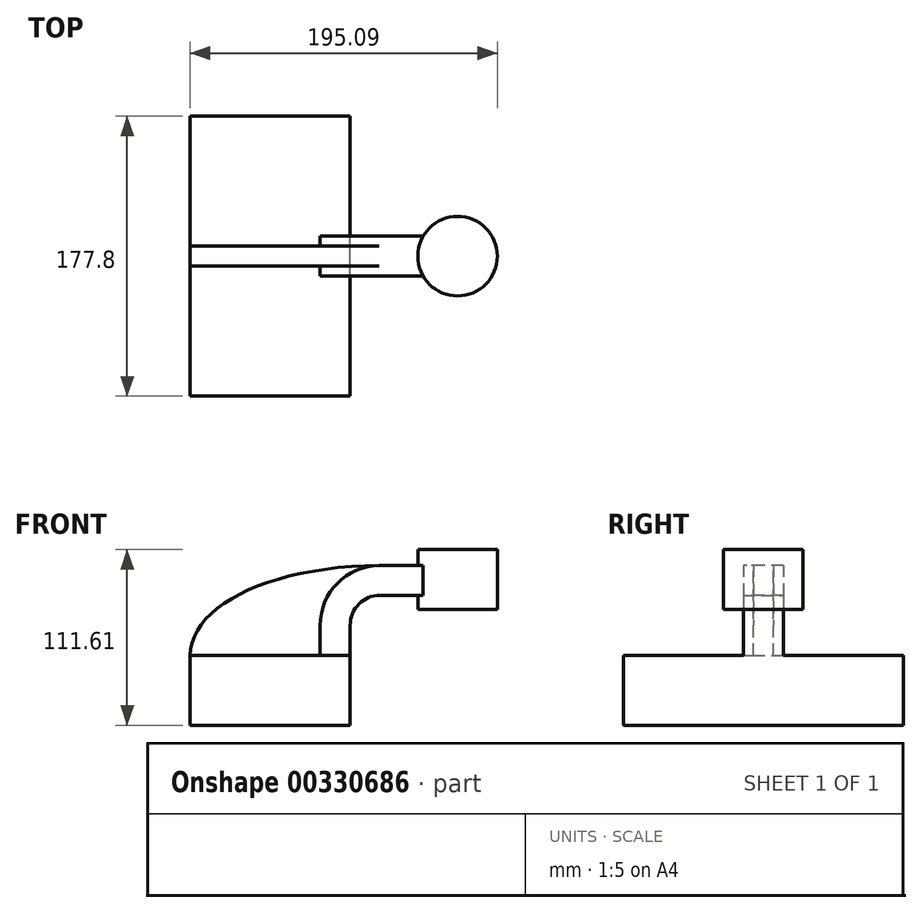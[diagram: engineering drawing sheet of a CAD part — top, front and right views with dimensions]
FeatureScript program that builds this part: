
annotation { "Feature Type Name" : "Feature", "Feature Type Description" : "" }
export const myFeature = defineFeature(function(context is Context, id is Id, definition is map)
    precondition{}
    {
        {
            var Q0;
            Q0=qCreatedBy(makeId("Front.planeOp"),FACE);
            var sketch = newSketch(context, id + "F0", { "sketchPlane" : qUnion([Q0])});
            skLineSegment(sketch, "E0.bottom", {"start": v(-50.8, 22.23) * mm, "end": v(50.8, 22.23) * mm});
            skLineSegment(sketch, "E0.top", {"start": v(-50.8, -22.23) * mm, "end": v(50.8, -22.23) * mm});
            skLineSegment(sketch, "E0.left", {"start": v(-50.8, 22.23) * mm, "end": v(-50.8, -22.23) * mm});
            skLineSegment(sketch, "E0.right", {"start": v(50.8, 22.23) * mm, "end": v(50.8, -22.23) * mm});
            skPoint(sketch, "E0.middle", {"position": v(0, 0) * mm});
            skLineSegment(sketch, "E1.bottom", {"start": v(93.5, 89.38) * mm, "end": v(144.3, 89.38) * mm});
            skLineSegment(sketch, "E1.top", {"start": v(93.5, 51.28) * mm, "end": v(144.3, 51.28) * mm});
            skLineSegment(sketch, "E1.left", {"start": v(93.5, 89.38) * mm, "end": v(93.5, 51.28) * mm});
            skLineSegment(sketch, "E1.right", {"start": v(144.3, 89.38) * mm, "end": v(144.3, 51.28) * mm});
            skPoint(sketch, "E1.middle", {"position": v(118.9, 70.33) * mm});
            skLineSegment(sketch, "E2", {"start": v(50.8, 22.23) * mm, "end": v(50.8, 41.28) * mm});
            skArc(sketch, "E3", {"start": v(50.8, 41.28) * mm, "mid": v(56.38, 54.75) * mm, "end": v(69.85, 60.33) * mm});
            skLineSegment(sketch, "E4", {"start": v(69.85, 60.33) * mm, "end": v(119, 60.33) * mm});
            skLineSegment(sketch, "E5.0", {"start": v(69.85, 79.38) * mm, "end": v(118.73, 79.38) * mm});
            skArc(sketch, "E5.1", {"start": v(31.75, 41.28) * mm, "mid": v(42.9, 68.22) * mm, "end": v(69.85, 79.38) * mm});
            skLineSegment(sketch, "E5.2", {"start": v(31.75, 22.23) * mm, "end": v(31.75, 41.28) * mm});
            skLineSegment(sketch, "E6", {"start": v(119, 60.33) * mm, "end": v(118.73, 79.38) * mm});
            skLineSegment(sketch, "E7", {"start": v(119.01, 51.28) * mm, "end": v(119.01, 89.38) * mm});
            skFitSpline(sketch, "E8", {"points": [v(-50.8, 22.22) * mm, v(69.85, 79.38) * mm], "startDerivative": vector(1.14, 94.53) * mm, "endDerivative": vector(209.55, 1.52) * mm});
            skSolve(sketch);
        }
        {
            var Q0;
            Q0=makeQuery(id+"F0.imprint","IMPRINT",FACE,{"disambiguationData":[TD([[makeQuery(id+"F0.imprint","IMPRINT",EDGE,{"derivedFrom":sQuery(id+"F0.wireOp",EDGE,"E0.top")}),1.0]])]});
            extrude(context, id + "F1", {"entities" : qUnion([Q0]), "endBound" : BoundingType.SYMMETRIC, "depth" : 177.8 * mm});
        }
        {
            var Q0;
            {var subQ3=sQuery(id+"F0.wireOp",EDGE,"E5.2");Q0=makeQuery(id+"F0.imprint","IMPRINT",FACE,{"disambiguationData":[TD([[makeQuery(id+"F0.imprint","IMPRINT",EDGE,{"derivedFrom":subQ3}),1.0]])]});}
            extrude(context, id + "F2", {"entities" : qUnion([Q0]), "operationType" : NewBodyOperationType.ADD, "endBound" : BoundingType.SYMMETRIC, "depth" : 12.7 * mm});
        }
        {
            var Q0;
            {var subQ1=sQuery(id+"F0.wireOp",EDGE,"E2");Q0=makeQuery(id+"F0.imprint","IMPRINT",FACE,{"disambiguationData":[TD([[makeQuery(id+"F0.imprint","IMPRINT",EDGE,{"derivedFrom":subQ1}),1.0]])]});}
            var Q1;
            {var subQ5=sQuery(id+"F0.wireOp",EDGE,"E6");Q1=makeQuery(id+"F0.imprint","IMPRINT",FACE,{"disambiguationData":[TD([[makeQuery(id+"F0.imprint","IMPRINT",EDGE,{"derivedFrom":subQ5}),1.0]])]});}
            extrude(context, id + "F3", {"entities" : qUnion([Q0, Q1]), "operationType" : NewBodyOperationType.ADD, "endBound" : BoundingType.SYMMETRIC, "depth" : 25.4 * mm});
        }
        {
            var Q0;
            {var subQ0=sQuery(id+"F0.wireOp",EDGE,"E1.right");Q0=makeQuery(id+"F0.imprint","IMPRINT",FACE,{"disambiguationData":[TD([[makeQuery(id+"F0.imprint","IMPRINT",EDGE,{"derivedFrom":subQ0}),-1.0]])]});}
            var Q1;
            Q1=sQuery(id+"F0.wireOp",EDGE,"E7");
            revolve(context, id + "F4", {"operationType" : NewBodyOperationType.ADD, "entities" : qUnion([Q0]), "axis" : qUnion([Q1]), "revolveType" : RevolveType.FULL});
        }
    });
